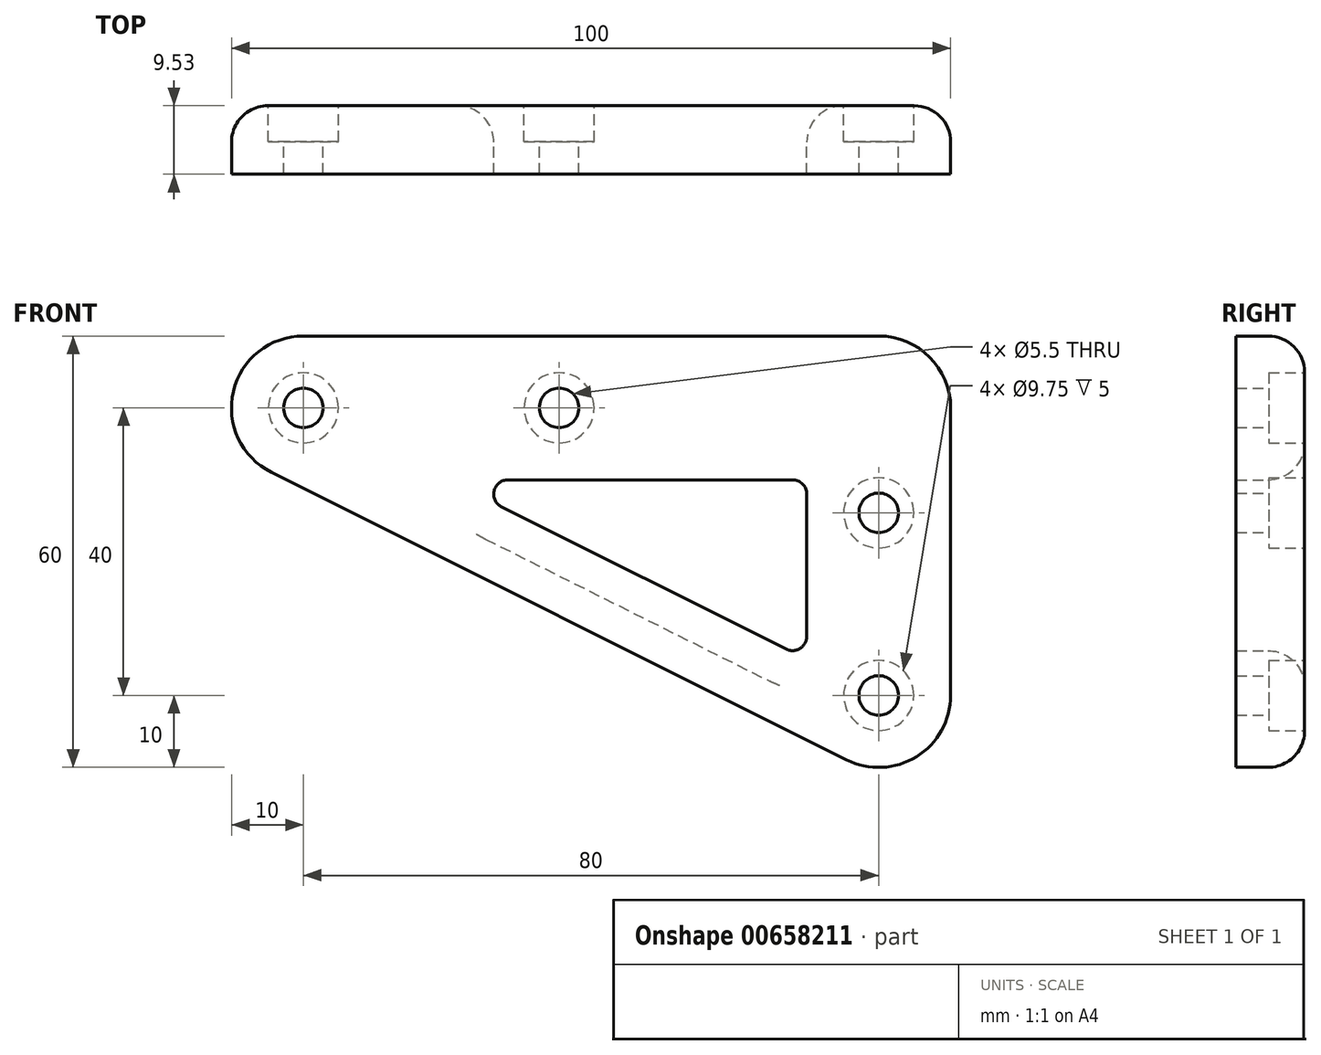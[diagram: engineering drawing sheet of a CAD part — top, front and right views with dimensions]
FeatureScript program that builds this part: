
annotation { "Feature Type Name" : "Feature", "Feature Type Description" : "" }
export const myFeature = defineFeature(function(context is Context, id is Id, definition is map)
    precondition{}
    {
        {
            var Q0;
            Q0=qCreatedBy(makeId("Front.planeOp"),FACE);
            var sketch = newSketch(context, id + "F0", { "sketchPlane" : qUnion([Q0])});
            skPoint(sketch, "E0.MirrorP", {"position": v(-44.44, 0) * mm});
            skArc(sketch, "E1", {"start": v(10, 0) * mm, "mid": v(7.07, 7.07) * mm, "end": v(0, 10) * mm});
            skPoint(sketch, "E2", {"position": v(0, -40) * mm});
            skArc(sketch, "E3", {"start": v(-4.47, -48.94) * mm, "mid": v(5.26, -48.5) * mm, "end": v(10, -40) * mm});
            skArc(sketch, "E4", {"start": v(-80, 10) * mm, "mid": v(-89.73, 2.3) * mm, "end": v(-84.47, -8.94) * mm});
            skLineSegment(sketch, "E5", {"start": v(-84.47, -8.94) * mm, "end": v(-4.47, -48.94) * mm});
            skLineSegment(sketch, "E6", {"start": v(-80, 10) * mm, "end": v(0, 10) * mm});
            skLineSegment(sketch, "E7", {"start": v(10, -40) * mm, "end": v(10, 0) * mm});
            skLineSegment(sketch, "E8.0", {"start": v(-52.42, -13.79) * mm, "end": v(-12.9, -33.55) * mm});
            skLineSegment(sketch, "E9.0", {"start": v(-10, -31.76) * mm, "end": v(-10, -12) * mm});
            skLineSegment(sketch, "E10.0", {"start": v(-51.53, -10) * mm, "end": v(-12, -10) * mm});
            skPoint(sketch, "E11.visualSharp", {"position": v(-60, -10) * mm});
            skArc(sketch, "E11.filletArc", {"start": v(-51.53, -10) * mm, "mid": v(-53.47, -11.54) * mm, "end": v(-52.42, -13.79) * mm});
            skPoint(sketch, "E12.visualSharp", {"position": v(-10, -10) * mm});
            skArc(sketch, "E12.filletArc", {"start": v(-10, -12) * mm, "mid": v(-10.59, -10.59) * mm, "end": v(-12, -10) * mm});
            skPoint(sketch, "E13.visualSharp", {"position": v(-10, -35) * mm});
            skArc(sketch, "E13.filletArc", {"start": v(-12.9, -33.55) * mm, "mid": v(-10.95, -33.47) * mm, "end": v(-10, -31.76) * mm});
            skPoint(sketch, "E14", {"position": v(0, -14.6) * mm});
            skSolve(sketch);
        }
        {
            var Q0;
            Q0 = qSketchRegion(id + "F0", true);
            extrude(context, id + "F1", {"entities" : qUnion([Q0]), "depth" : 9.52 * mm, "offsetDistance" : 25.4 * mm});
        }
        {
            var Q0;
            Q0=sQuery(id+"F0.wireOp",VERTEX,"E2");
            var Q1;
            Q1=sQuery(id+"F0.wireOp",VERTEX,"E0.MirrorP");
            var Q2;
            Q2=sQuery(id+"F0.wireOp",VERTEX,"E4.center");
            var Q3;
            Q3=sQuery(id+"F0.wireOp",VERTEX,"E14");
            var Q4;
            Q4=makeQuery(id+"F1.opExtrude","SWEPT_BODY",BODY,{"disambiguationData":[OSD([sQuery(id+"F0.wireOp",EDGE,"bf2f238d-4e1d-4e86-ab75-1465cd813df2.MirrorCS"),sQuery(id+"F0.wireOp",EDGE,"7d5bedbb-471c-4160-8e68-eb1f4d767648.MirrorCS"),sQuery(id+"F0.wireOp",EDGE,"bc7fee83-9e46-4c51-805a-8ae9689402aa.MirrorCS"),sQuery(id+"F0.wireOp",EDGE,"e5d497b7-cccf-4703-a1dc-18e520bbeae9.MirrorCS"),sQuery(id+"F0.wireOp",EDGE,"c155fd9a-5cc5-4759-a1c6-071fd15af197.MirrorCS"),sQuery(id+"F0.wireOp",EDGE,"33a989d6-5cc4-4172-ab73-ca817da9f412.MirrorCS"),sQuery(id+"F0.wireOp",EDGE,"1c3aec17-fec7-453e-8acd-3df81b9bc4e3.MirrorCS"),sQuery(id+"F0.wireOp",EDGE,"0cd19f4d-6d86-4b4a-a093-bb589b475590.MirrorCS"),sQuery(id+"F0.wireOp",EDGE,"eee5d6f5-912f-4719-99ba-1d72e724f1e9.MirrorCS"),sQuery(id+"F0.wireOp",EDGE,"64a401ff-d109-42b1-96b9-6f7f2e519c4d.MirrorCS"),sQuery(id+"F0.wireOp",EDGE,"2bc110f3-ae92-45de-b2b7-7df43831b8ab"),sQuery(id+"F0.wireOp",EDGE,"pibmvETk-c1Xj-BIgN-8uma-1jo4IxxjolSW")])]});
            var Q5;
            Q5=makeQuery(id+"F1.opExtrude","SWEPT_BODY",BODY,{"disambiguationData":[OSD([sQuery(id+"F0.wireOp",EDGE,"E1"),sQuery(id+"F0.wireOp",EDGE,"E3"),sQuery(id+"F0.wireOp",EDGE,"E4"),sQuery(id+"F0.wireOp",EDGE,"E5"),sQuery(id+"F0.wireOp",EDGE,"E6"),sQuery(id+"F0.wireOp",EDGE,"E7"),sQuery(id+"F0.wireOp",EDGE,"E8.0"),sQuery(id+"F0.wireOp",EDGE,"E9.0"),sQuery(id+"F0.wireOp",EDGE,"E10.0"),sQuery(id+"F0.wireOp",EDGE,"E11.filletArc"),sQuery(id+"F0.wireOp",EDGE,"E12.filletArc"),sQuery(id+"F0.wireOp",EDGE,"E13.filletArc")])]});
            hole(context, id + "F2", {"style" : HoleStyle.C_BORE, "endStyle" : HoleEndStyle.THROUGH, "oppositeDirection" : true, "standardTappedOrClearance" : lookupTablePath({ "standard" : "ISO", "fit" : "Normal", "size" : "M5", "type" : "Clearance" }), "standardBlindInLast" : lookupTablePath({ "fit" : "Standard", "standard" : "ISO", "size" : "M5", "type" : "Clearance" }), "holeDiameter" : 5.5 * mm, "cBoreDiameter" : 9.75 * mm, "cBoreDepth" : 5 * mm, "majorDiameter" : 6.35 * mm, "isTappedThrough" : true, "tappedDepth" : 12.7 * mm, "tapClearance" : 3, "locations" : qUnion([Q0, Q1, Q2, Q3]), "scope" : qUnion([Q4, Q5])});
        }
        {
            var Q0;
            Q0=makeQuery(id+"F1.opExtrude","CAP_EDGE",EDGE,{"disambiguationData":[OSD([sQuery(id+"F0.wireOp",EDGE,"E6")])],"isStart":true});
            var Q1;
            Q1=makeQuery(id+"F1.opExtrude","CAP_EDGE",EDGE,{"disambiguationData":[OSD([sQuery(id+"F0.wireOp",EDGE,"E10.0")])],"isStart":true});
            fillet(context, id + "F3", {"entities" : qUnion([Q0, Q1]), "radius" : 5.08 * mm, "tangentPropagation" : true, "allowEdgeOverflow" : false});
        }
    });
